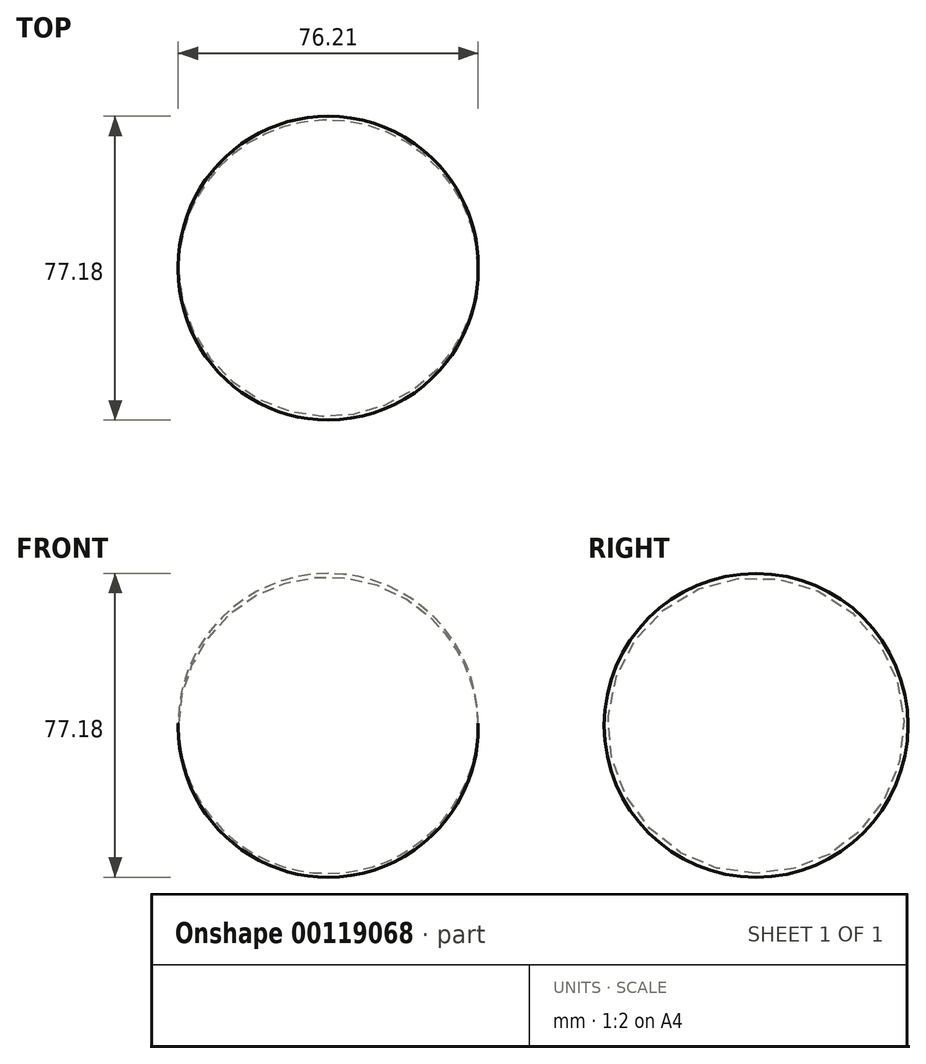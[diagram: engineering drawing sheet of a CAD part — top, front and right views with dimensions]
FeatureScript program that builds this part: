
annotation { "Feature Type Name" : "Feature", "Feature Type Description" : "" }
export const myFeature = defineFeature(function(context is Context, id is Id, definition is map)
    precondition{}
    {
        {
            var Q0;
            Q0=qCreatedBy(makeId("Front.planeOp"),FACE);
            var sketch = newSketch(context, id + "F0", { "sketchPlane" : qUnion([Q0])});
            skLineSegment(sketch, "E0", {"start": v(-37.85, 0) * mm, "end": v(38.35, 0) * mm});
            skArc(sketch, "E1", {"start": v(38.35, 0) * mm, "mid": v(0.25, 37.62) * mm, "end": v(-37.85, 0) * mm});
            skSolve(sketch);
        }
        {
            var Q0;
            Q0 = qSketchRegion(id + "F0", true);
            var Q1;
            Q1=sQuery(id+"F0.wireOp",EDGE,"E0");
            revolve(context, id + "F1", {"entities" : qUnion([Q0]), "axis" : qUnion([Q1]), "revolveType" : RevolveType.FULL});
        }
    });
